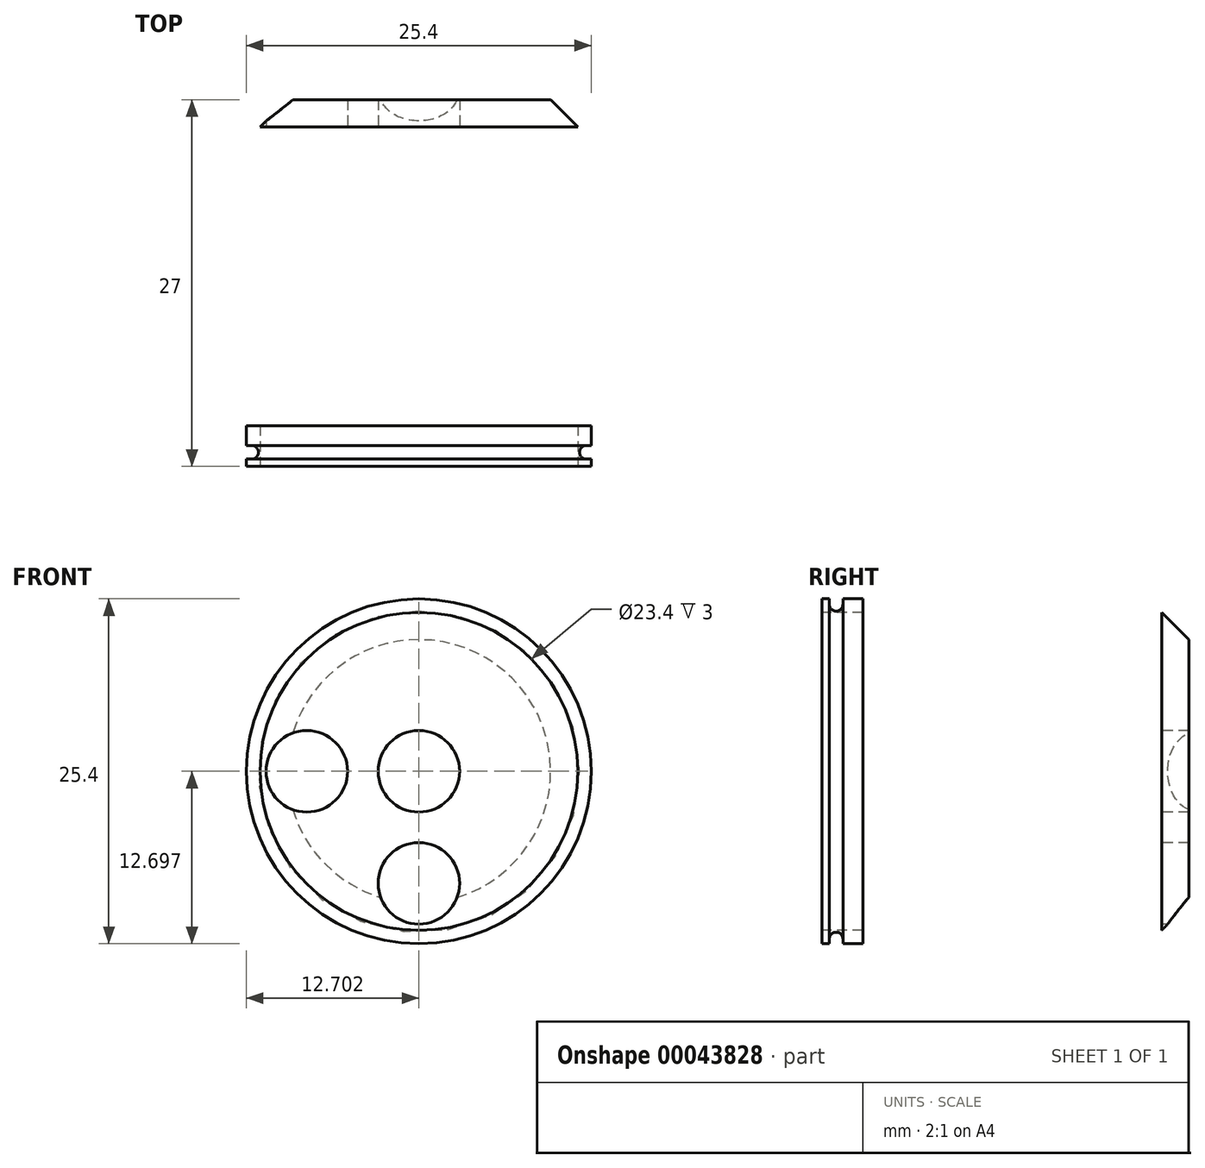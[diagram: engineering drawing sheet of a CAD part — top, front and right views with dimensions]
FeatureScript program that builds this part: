
annotation { "Feature Type Name" : "Feature", "Feature Type Description" : "" }
export const myFeature = defineFeature(function(context is Context, id is Id, definition is map)
    precondition{}
    {
        {
            var Q0;
            Q0=qCreatedBy(makeId("Front.planeOp"),FACE);
            var sketch = newSketch(context, id + "F0", { "sketchPlane" : qUnion([Q0])});
            skCircle(sketch, "E0", {"center": v(0, 0.03) * mm, "radius": 3 * mm});
            skLineSegment(sketch, "E1", {"start": v(0, 0.03) * mm, "end": v(25.08, 0.03) * mm, "construction": true});
            skLineSegment(sketch, "E2", {"start": v(0, 0.03) * mm, "end": v(0, -21.89) * mm, "construction": true});
            skCircle(sketch, "E3", {"center": v(8.24, 0.03) * mm, "radius": 3 * mm});
            skCircle(sketch, "E4.MirrorC", {"center": v(-8.26, 0.03) * mm, "radius": 3 * mm});
            skCircle(sketch, "E5", {"center": v(0, 0.03) * mm, "radius": 12.7 * mm});
            skCircle(sketch, "E6", {"center": v(0, 0.03) * mm, "radius": 8.25 * mm, "construction": true});
            skCircle(sketch, "E7", {"center": v(0, 8.28) * mm, "radius": 3 * mm});
            skCircle(sketch, "E8.MirrorC", {"center": v(0, -8.22) * mm, "radius": 3 * mm});
            skCircle(sketch, "E9.0", {"center": v(0, 0.03) * mm, "radius": 11.7 * mm});
            skSolve(sketch);
        }
        {
            var Q0;
            Q0=makeQuery(id+"F0.imprint","IMPRINT",FACE,{"disambiguationData":[TD([[makeQuery(id+"F0.imprint","IMPRINT",EDGE,{"derivedFrom":sQuery(id+"F0.wireOp",EDGE,"E0")}),-1.0]])]});
            var Q1;
            Q1=makeQuery(id+"F0.imprint","IMPRINT",FACE,{"disambiguationData":[TD([[makeQuery(id+"F0.imprint","IMPRINT",EDGE,{"derivedFrom":sQuery(id+"F0.wireOp",EDGE,"E5")}),1.0]])]});
            var Q2;
            Q2=makeQuery(id+"F0.imprint","IMPRINT",FACE,{"disambiguationData":[TD([[makeQuery(id+"F0.imprint","IMPRINT",EDGE,{"derivedFrom":sQuery(id+"F0.wireOp",EDGE,"E4.MirrorC")}),-1.0]])]});
            var Q3;
            Q3=makeQuery(id+"F0.imprint","IMPRINT",FACE,{"disambiguationData":[TD([[makeQuery(id+"F0.imprint","IMPRINT",EDGE,{"derivedFrom":sQuery(id+"F0.wireOp",EDGE,"E8.MirrorC")}),-1.0]])]});
            var Q4;
            Q4=makeQuery(id+"F0.imprint","IMPRINT",FACE,{"disambiguationData":[TD([[makeQuery(id+"F0.imprint","IMPRINT",EDGE,{"derivedFrom":sQuery(id+"F0.wireOp",EDGE,"E3")}),1.0]])]});
            var Q5;
            Q5=makeQuery(id+"F0.imprint","IMPRINT",FACE,{"disambiguationData":[TD([[makeQuery(id+"F0.imprint","IMPRINT",EDGE,{"derivedFrom":sQuery(id+"F0.wireOp",EDGE,"E7")}),1.0]])]});
            extrude(context, id + "F1", {"entities" : qUnion([Q0, Q1, Q2, Q3, Q4, Q5]), "oppositeDirection" : true, "depth" : 3 * mm});
        }
        {
            var Q0;
            Q0=makeQuery(id+"F0.imprint","IMPRINT",FACE,{"disambiguationData":[TD([[makeQuery(id+"F0.imprint","IMPRINT",EDGE,{"derivedFrom":sQuery(id+"F0.wireOp",EDGE,"E0")}),-1.0]])]});
            var Q1;
            Q1=makeQuery(id+"F0.imprint","IMPRINT",FACE,{"disambiguationData":[TD([[makeQuery(id+"F0.imprint","IMPRINT",EDGE,{"derivedFrom":sQuery(id+"F0.wireOp",EDGE,"E4.MirrorC")}),-1.0]])]});
            var Q2;
            Q2=makeQuery(id+"F0.imprint","IMPRINT",FACE,{"disambiguationData":[TD([[makeQuery(id+"F0.imprint","IMPRINT",EDGE,{"derivedFrom":sQuery(id+"F0.wireOp",EDGE,"E7")}),1.0]])]});
            var Q3;
            Q3=makeQuery(id+"F0.imprint","IMPRINT",FACE,{"disambiguationData":[TD([[makeQuery(id+"F0.imprint","IMPRINT",EDGE,{"derivedFrom":sQuery(id+"F0.wireOp",EDGE,"E3")}),1.0]])]});
            var Q4;
            Q4=makeQuery(id+"F0.imprint","IMPRINT",FACE,{"disambiguationData":[TD([[makeQuery(id+"F0.imprint","IMPRINT",EDGE,{"derivedFrom":sQuery(id+"F0.wireOp",EDGE,"E8.MirrorC")}),-1.0]])]});
            extrude(context, id + "F2", {"entities" : qUnion([Q0, Q1, Q2, Q3, Q4]), "operationType" : NewBodyOperationType.ADD, "oppositeDirection" : true, "depth" : 27 * mm});
        }
        {
            var Q0;
            Q0=makeQuery(id+"F0.imprint","IMPRINT",FACE,{"disambiguationData":[TD([[makeQuery(id+"F0.imprint","IMPRINT",EDGE,{"derivedFrom":sQuery(id+"F0.wireOp",EDGE,"E4.MirrorC")}),-1.0]])]});
            var Q1;
            Q1=makeQuery(id+"F0.imprint","IMPRINT",FACE,{"disambiguationData":[TD([[makeQuery(id+"F0.imprint","IMPRINT",EDGE,{"derivedFrom":sQuery(id+"F0.wireOp",EDGE,"E7")}),1.0]])]});
            var Q2;
            Q2=makeQuery(id+"F0.imprint","IMPRINT",FACE,{"disambiguationData":[TD([[makeQuery(id+"F0.imprint","IMPRINT",EDGE,{"derivedFrom":sQuery(id+"F0.wireOp",EDGE,"E3")}),1.0]])]});
            var Q3;
            Q3=makeQuery(id+"F0.imprint","IMPRINT",FACE,{"disambiguationData":[TD([[makeQuery(id+"F0.imprint","IMPRINT",EDGE,{"derivedFrom":sQuery(id+"F0.wireOp",EDGE,"E8.MirrorC")}),-1.0]])]});
            extrude(context, id + "F3", {"entities" : qUnion([Q0, Q1, Q2, Q3]), "operationType" : NewBodyOperationType.REMOVE, "oppositeDirection" : true, "depth" : 25 * mm});
        }
        {
            var Q0;
            Q0=qCreatedBy(makeId("Top.planeOp"),FACE);
            var sketch = newSketch(context, id + "F4", { "sketchPlane" : qUnion([Q0])});
            skLineSegment(sketch, "E10", {"start": v(0, 0) * mm, "end": v(17.82, 0) * mm});
            skLineSegment(sketch, "E11.0", {"start": v(-1.5, 11.5) * mm, "end": v(-1.5, 4.5) * mm});
            skLineSegment(sketch, "E12.0", {"start": v(1.5, 11.5) * mm, "end": v(1.5, 4.5) * mm});
            skArc(sketch, "E13", {"start": v(-1.5, 4.5) * mm, "mid": v(0, 3) * mm, "end": v(1.5, 4.5) * mm});
            skArc(sketch, "E14", {"start": v(1.5, 11.5) * mm, "mid": v(0, 13) * mm, "end": v(-1.5, 11.5) * mm});
            skSolve(sketch);
        }
        {
            var Q0;
            Q0 = qSketchRegion(id + "F4", true);
            extrude(context, id + "F5", {"entities" : qUnion([Q0]), "operationType" : NewBodyOperationType.REMOVE, "endBound" : BoundingType.SYMMETRIC, "oppositeDirection" : true, "depth" : 30 * mm});
        }
        {
            var Q0;
            Q0=qCreatedBy(makeId("Right.planeOp"),FACE);
            var sketch = newSketch(context, id + "F6", { "sketchPlane" : qUnion([Q0])});
            skLineSegment(sketch, "E15", {"start": v(3.03, 0) * mm, "end": v(3.03, 1.5) * mm});
            skLineSegment(sketch, "E16.0", {"start": v(4.53, -1.5) * mm, "end": v(11.53, -1.5) * mm});
            skArc(sketch, "E17", {"start": v(4.53, 1.5) * mm, "mid": v(3.03, 0) * mm, "end": v(4.53, -1.5) * mm});
            skArc(sketch, "E18", {"start": v(11.53, -1.5) * mm, "mid": v(13.03, 0) * mm, "end": v(11.53, 1.5) * mm});
            skLineSegment(sketch, "E19.trimOffspring", {"start": v(4.53, 1.5) * mm, "end": v(11.53, 1.5) * mm});
            skSolve(sketch);
        }
        {
            var Q0;
            Q0 = qSketchRegion(id + "F6", true);
            extrude(context, id + "F7", {"entities" : qUnion([Q0]), "operationType" : NewBodyOperationType.REMOVE, "endBound" : BoundingType.SYMMETRIC, "oppositeDirection" : true, "depth" : 30 * mm});
        }
        {
            var Q0;
            Q0=qCreatedBy(makeId("Top.planeOp"),FACE);
            var sketch = newSketch(context, id + "F8", { "sketchPlane" : qUnion([Q0])});
            skLineSegment(sketch, "E20", {"start": v(-12.72, 3.34) * mm, "end": v(-12.72, 1.54) * mm});
            skLineSegment(sketch, "E21", {"start": v(0, 0) * mm, "end": v(0, 2.56) * mm});
            skLineSegment(sketch, "E22.0", {"start": v(-12.32, 3.34) * mm, "end": v(-12.32, 1.54) * mm});
            skArc(sketch, "E23", {"start": v(-12.32, 0.54) * mm, "mid": v(-11.82, 1.04) * mm, "end": v(-12.32, 1.54) * mm});
            skLineSegment(sketch, "E24", {"start": v(-12.32, 1.54) * mm, "end": v(-13.74, 1.54) * mm});
            skLineSegment(sketch, "E25", {"start": v(-12.32, 0.54) * mm, "end": v(-13.74, 0.54) * mm});
            skLineSegment(sketch, "E26", {"start": v(-13.74, 1.54) * mm, "end": v(-13.74, 0.54) * mm});
            skLineSegment(sketch, "E27.trimOffspring", {"start": v(-12.72, 1.34) * mm, "end": v(-12.72, 0.74) * mm});
            skLineSegment(sketch, "E28.trimOffspring", {"start": v(-12.32, 0.54) * mm, "end": v(-12.32, -2.6) * mm});
            skSolve(sketch);
        }
        {
            var Q0;
            Q0 = qSketchRegion(id + "F8", true);
            var Q1;
            Q1=sQuery(id+"F8.wireOp",EDGE,"E21");
            revolve(context, id + "F9", {"operationType" : NewBodyOperationType.REMOVE, "entities" : qUnion([Q0]), "axis" : qUnion([Q1]), "revolveType" : RevolveType.FULL, "oppositeDirection" : true});
        }
        {
            var Q0;
            Q0 = qSketchRegion(id + "F8", true);
            var Q1;
            Q1=sQuery(id+"F8.wireOp",EDGE,"E21");
            revolve(context, id + "F10", {"operationType" : NewBodyOperationType.REMOVE, "entities" : qUnion([Q0]), "axis" : qUnion([Q1]), "revolveType" : RevolveType.FULL});
        }
        {
            var Q0;
            Q0=makeQuery(id+"F2.opExtrude","CAP_EDGE",EDGE,{"disambiguationData":[OSD([sQuery(id+"F0.wireOp",EDGE,"E9.0")])],"isStart":false});
            chamfer(context, id + "F11", {"entities" : qUnion([Q0]), "width" : 2 * mm, "tangentPropagation" : true});
        }
    });
